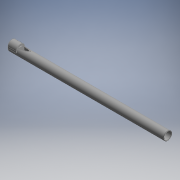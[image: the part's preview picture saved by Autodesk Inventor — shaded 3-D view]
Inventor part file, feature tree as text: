
AUTODESK INVENTOR PART (.ipt)
format: ipt  version: 2018 (Build 220112000, 112)  size: 304,128 bytes
history: native  units: in
note: dims shown in document units (in); Inventor stores cm internally (conversion verified against a paired STEP export)
features: extrude x4, other x4, fillet x3
ambient origin geometry x8: Origin, YZ Plane, XZ Plane, XY Plane, X Axis, Y Axis, Z Axis, Center Point
bodies: Solid1 (feature_tree)
feature tree (11):
  extrude  "Tube"  TaperAngle=0.0deg  [1 undecoded]
  extrude  "Cap"  Depth=0.3937in TaperAngle=0.0deg
  extrude  "Edge Cut"  Depth=0.3937in TaperAngle=0.0deg
  extrude  "Slit"  Depth=0.0079in
  fillet  "Fillet1"  Radius=0.0079in
  fillet  "Fillet2"  [1 undecoded]
  fillet  "Fillet3"  [1 undecoded]
  other  "Tube Sketch"
  other  "Cap Shape"
  other  ",Edge Cut Sketch"
  other  "Slit Sketch"
note: 3 required parameter values undecoded (feature->parameter linkage not recoverable at this tier; creation-order binding heuristic only, values carry confidence <= 0.55)
